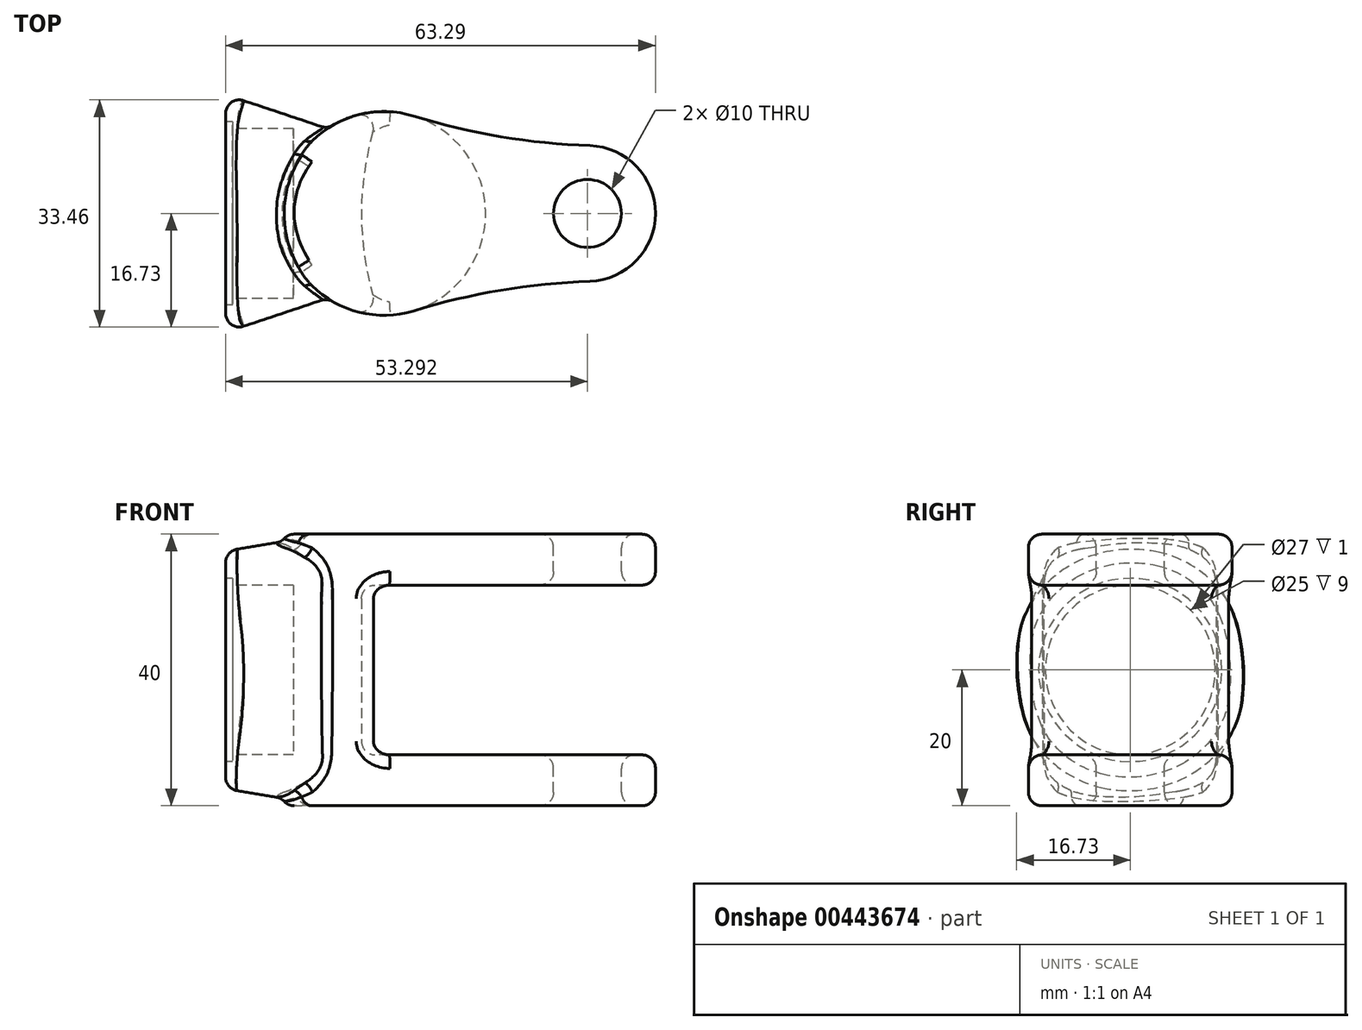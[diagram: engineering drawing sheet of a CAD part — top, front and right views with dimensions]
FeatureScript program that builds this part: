
annotation { "Feature Type Name" : "Feature", "Feature Type Description" : "" }
export const myFeature = defineFeature(function(context is Context, id is Id, definition is map)
    precondition{}
    {
        {
            var Q0;
            Q0=qCreatedBy(makeId("Right.planeOp"),FACE);
            var sketch = newSketch(context, id + "F0", { "sketchPlane" : qUnion([Q0])});
            skCircle(sketch, "E0", {"center": v(0, 0) * mm, "radius": 17.5 * mm});
            skSolve(sketch);
        }
        {
            var Q0;
            Q0=makeQuery(id+"F0.imprint","IMPRINT",FACE,{"disambiguationData":[TD([[makeQuery(id+"F0.imprint","IMPRINT",EDGE,{"derivedFrom":sQuery(id+"F0.wireOp",EDGE,"E0")}),1.0]])]});
            cPlane(context, id + "F1", {"entities" : qUnion([Q0]), "cplaneType" : CPlaneType.OFFSET, "offset" : 15 * mm, "width" : 150 * mm, "height" : 150 * mm});
        }
        {
            var Q0;
            Q0=qCreatedBy(id+"F1.planeOp",FACE);
            var sketch = newSketch(context, id + "F2", { "sketchPlane" : qUnion([Q0])});
            skLineSegment(sketch, "E1.bottom", {"start": v(-5, -20) * mm, "end": v(5, -20) * mm});
            skLineSegment(sketch, "E1.top", {"start": v(-5, 20) * mm, "end": v(5, 20) * mm});
            skLineSegment(sketch, "E1.left", {"start": v(-12.5, -12.5) * mm, "end": v(-12.5, 12.5) * mm});
            skLineSegment(sketch, "E1.right", {"start": v(12.5, -12.5) * mm, "end": v(12.5, 12.5) * mm});
            skPoint(sketch, "E1.middle", {"position": v(0, 0) * mm});
            skPoint(sketch, "E2.visualSharp", {"position": v(-12.5, -20) * mm});
            skArc(sketch, "E2.filletArc", {"start": v(-12.5, -12.5) * mm, "mid": v(-10.3, -17.8) * mm, "end": v(-5, -20) * mm});
            skPoint(sketch, "E3.visualSharp", {"position": v(12.5, -20) * mm});
            skArc(sketch, "E3.filletArc", {"start": v(5, -20) * mm, "mid": v(10.3, -17.8) * mm, "end": v(12.5, -12.5) * mm});
            skPoint(sketch, "E4.visualSharp", {"position": v(-12.5, 20) * mm});
            skArc(sketch, "E4.filletArc", {"start": v(-5, 20) * mm, "mid": v(-10.3, 17.8) * mm, "end": v(-12.5, 12.5) * mm});
            skPoint(sketch, "E5.visualSharp", {"position": v(12.5, 20) * mm});
            skArc(sketch, "E5.filletArc", {"start": v(12.5, 12.5) * mm, "mid": v(10.3, 17.8) * mm, "end": v(5, 20) * mm});
            skSolve(sketch);
        }
        {
            var Q0;
            Q0=makeQuery(id+"F0.imprint","IMPRINT",FACE,{"disambiguationData":[TD([[makeQuery(id+"F0.imprint","IMPRINT",EDGE,{"derivedFrom":sQuery(id+"F0.wireOp",EDGE,"E0")}),1.0]])]});
            var Q1;
            Q1=makeQuery(id+"F2.imprint","IMPRINT",FACE,{"disambiguationData":[TD([[makeQuery(id+"F2.imprint","IMPRINT",EDGE,{"derivedFrom":sQuery(id+"F2.wireOp",EDGE,"E1.bottom")}),1.0]])]});
            loft(context, id + "F3", {"sheetProfilesArray" : [{ "sheetProfileEntities" : qUnion([Q0]) }, { "sheetProfileEntities" : qUnion([Q1]) }]});
        }
        {
            var Q0;
            Q0=qCreatedBy(makeId("Top.planeOp"),FACE);
            var sketch = newSketch(context, id + "F4", { "sketchPlane" : qUnion([Q0])});
            skArc(sketch, "E6", {"start": v(27.7, 14.34) * mm, "mid": v(8.3, 0) * mm, "end": v(27.7, -14.34) * mm});
            skArc(sketch, "E7", {"start": v(53.63, -10) * mm, "mid": v(63.3, 0) * mm, "end": v(53.63, 10) * mm});
            skLineSegment(sketch, "E8", {"start": v(23.3, 0) * mm, "end": v(53.3, 0) * mm, "construction": true});
            skArc(sketch, "E9", {"start": v(27.7, 14.34) * mm, "mid": v(40.52, 11.31) * mm, "end": v(53.63, 10) * mm});
            skArc(sketch, "E10.MirrorCS", {"start": v(27.7, -14.34) * mm, "mid": v(40.52, -11.31) * mm, "end": v(53.63, -10) * mm});
            skSolve(sketch);
        }
        {
            var Q0;
            Q0 = qSketchRegion(id + "F4", true);
            extrude(context, id + "F5", {"entities" : qUnion([Q0]), "operationType" : NewBodyOperationType.ADD, "endBound" : BoundingType.SYMMETRIC, "depth" : 40 * mm});
        }
        {
            var Q0;
            Q0=qCreatedBy(makeId("Front.planeOp"),FACE);
            var sketch = newSketch(context, id + "F6", { "sketchPlane" : qUnion([Q0])});
            skLineSegment(sketch, "E11.bottom", {"start": v(20, 12.5) * mm, "end": v(63.3, 12.5) * mm});
            skLineSegment(sketch, "E11.top", {"start": v(20, -12.5) * mm, "end": v(63.3, -12.5) * mm});
            skLineSegment(sketch, "E11.left", {"start": v(20, 12.5) * mm, "end": v(20, -12.5) * mm});
            skLineSegment(sketch, "E11.right", {"start": v(63.3, 12.5) * mm, "end": v(63.3, -12.5) * mm});
            skSolve(sketch);
        }
        {
            var Q0;
            Q0 = qSketchRegion(id + "F6", true);
            var Q1;
            Q1=sQuery(id+"F6.wireOp",EDGE,"E11.right");
            revolve(context, id + "F7", {"operationType" : NewBodyOperationType.REMOVE, "entities" : qUnion([Q0]), "axis" : qUnion([Q1]), "revolveType" : RevolveType.FULL, "oppositeDirection" : true});
        }
        {
            var Q0;
            Q0=makeQuery(id+"F3.opLoft","CAP_FACE",FACE,{"disambiguationData":[OSD([makeQuery(id+"F0.imprint","IMPRINT",FACE,{"disambiguationData":[TD([[makeQuery(id+"F0.imprint","IMPRINT",EDGE,{"derivedFrom":sQuery(id+"F0.wireOp",EDGE,"E0")}),1.0]])]})])],"isStart":true});
            var sketch = newSketch(context, id + "F8", { "sketchPlane" : qUnion([Q0])});
            skCircle(sketch, "E12", {"center": v(0, 0) * mm, "radius": 12.5 * mm});
            skSolve(sketch);
        }
        {
            var Q0;
            Q0 = qSketchRegion(id + "F8", true);
            extrude(context, id + "F9", {"entities" : qUnion([Q0]), "operationType" : NewBodyOperationType.REMOVE, "oppositeDirection" : true, "depth" : 10 * mm});
        }
        {
            var Q0;
            Q0=makeQuery(id+"F3.opLoft","CAP_FACE",FACE,{"disambiguationData":[OSD([makeQuery(id+"F0.imprint","IMPRINT",FACE,{"disambiguationData":[TD([[makeQuery(id+"F0.imprint","IMPRINT",EDGE,{"derivedFrom":sQuery(id+"F0.wireOp",EDGE,"E0")}),1.0]])]})])],"isStart":true});
            var sketch = newSketch(context, id + "F10", { "sketchPlane" : qUnion([Q0])});
            skCircle(sketch, "E13.0", {"center": v(0, 0) * mm, "radius": 13.5 * mm});
            skSolve(sketch);
        }
        {
            var Q0;
            Q0 = qSketchRegion(id + "F10", true);
            extrude(context, id + "F11", {"entities" : qUnion([Q0]), "operationType" : NewBodyOperationType.REMOVE, "oppositeDirection" : true, "depth" : 1 * mm});
        }
        {
            var Q0;
            Q0=makeQuery(id+"F5.opExtrude","CAP_FACE",FACE,{"disambiguationData":[OSD([sQuery(id+"F4.wireOp",EDGE,"E6"),sQuery(id+"F4.wireOp",EDGE,"E7"),sQuery(id+"F4.wireOp",EDGE,"E9"),sQuery(id+"F4.wireOp",EDGE,"E10.MirrorCS")])],"isStart":false});
            var sketch = newSketch(context, id + "F12", { "sketchPlane" : qUnion([Q0])});
            skCircle(sketch, "E14", {"center": v(53.3, 0) * mm, "radius": 5 * mm});
            skSolve(sketch);
        }
        {
            var Q0;
            Q0=makeQuery(id+"F12.imprint","IMPRINT",FACE,{"disambiguationData":[TD([[makeQuery(id+"F12.imprint","IMPRINT",EDGE,{"derivedFrom":sQuery(id+"F12.wireOp",EDGE,"E14")}),1.0]])]});
            extrude(context, id + "F13", {"entities" : qUnion([Q0]), "operationType" : NewBodyOperationType.REMOVE, "endBound" : BoundingType.THROUGH_ALL, "oppositeDirection" : true, "depth" : 25 * mm});
        }
        {
            var Q0;
            Q0=makeQuery(id+"F5.opExtrude","CAP_FACE",FACE,{"disambiguationData":[OSD([sQuery(id+"F4.wireOp",EDGE,"E6"),sQuery(id+"F4.wireOp",EDGE,"E7"),sQuery(id+"F4.wireOp",EDGE,"E9"),sQuery(id+"F4.wireOp",EDGE,"E10.MirrorCS")])],"isStart":false});
            var Q1;
            Q1=makeQuery(id+"F5.opExtrude","CAP_FACE",FACE,{"disambiguationData":[OSD([sQuery(id+"F4.wireOp",EDGE,"E6"),sQuery(id+"F4.wireOp",EDGE,"E7"),sQuery(id+"F4.wireOp",EDGE,"E9"),sQuery(id+"F4.wireOp",EDGE,"E10.MirrorCS")])],"isStart":true});
            var Q2;
            Q2=makeQuery(id+"F7.boolean.opBoolean","COPY",EDGE,{"derivedFrom":makeQuery(id+"F7.opRevolve","SWEPT_EDGE",EDGE,{"disambiguationData":[OSD([sQuery(id+"F6.wireOp",EDGE,"E11.bottom"),sQuery(id+"F6.wireOp",EDGE,"E11.left")])]})});
            var Q3;
            Q3=makeQuery(id+"F7.boolean.opBoolean","COPY",EDGE,{"derivedFrom":makeQuery(id+"F7.opRevolve","SWEPT_EDGE",EDGE,{"disambiguationData":[OSD([sQuery(id+"F6.wireOp",EDGE,"E11.top"),sQuery(id+"F6.wireOp",EDGE,"E11.left")])]})});
            fillet(context, id + "F14", {"entities" : qUnion([Q0, Q1, Q2, Q3]), "radius" : 2 * mm, "tangentPropagation" : true, "allowEdgeOverflow" : false});
        }
        {
            var Q0;
            Q0=makeQuery(id+"F7.boolean.opBoolean","COPY",FACE,{"derivedFrom":makeQuery(id+"F7.opRevolve","SWEPT_FACE",FACE,{"disambiguationData":[OSD([sQuery(id+"F6.wireOp",EDGE,"E11.top")])]})});
            var Q1;
            Q1=makeQuery(id+"F7.boolean.opBoolean","COPY",FACE,{"derivedFrom":makeQuery(id+"F7.opRevolve","SWEPT_FACE",FACE,{"disambiguationData":[OSD([sQuery(id+"F6.wireOp",EDGE,"E11.bottom")])]})});
            fillet(context, id + "F15", {"entities" : qUnion([Q0, Q1]), "radius" : 2 * mm, "tangentPropagation" : true, "allowEdgeOverflow" : false});
        }
        {
            var Q0;
            Q0=makeQuery(id+"F3.opLoft","MID_CAP_EDGE",EDGE,{"disambiguationData":[OSD([sQuery(id+"F2.wireOp",EDGE,"E1.right"),sQuery(id+"F2.wireOp",EDGE,"E3.filletArc"),sQuery(id+"F2.wireOp",EDGE,"E5.filletArc")])],"capPos":1.0});
            var Q1;
            Q1=makeQuery(id+"F5.boolean.opBoolean","INTERSECT",EDGE,{"disambiguationData":[OD(1.0)],"derivedFrom":[makeQuery(id+"F3.opLoft","SWEPT_FACE",FACE,{"disambiguationData":[OSD([sQuery(id+"F0.wireOp",EDGE,"E0"),sQuery(id+"F2.wireOp",EDGE,"E1.bottom"),sQuery(id+"F2.wireOp",EDGE,"E2.filletArc"),sQuery(id+"F2.wireOp",EDGE,"E3.filletArc")])]}),makeQuery(id+"F5.opExtrude","SWEPT_FACE",FACE,{"disambiguationData":[OSD([sQuery(id+"F4.wireOp",EDGE,"E6")])]})]});
            var Q2;
            Q2=makeQuery(id+"F3.opLoft","SWEPT_FACE",FACE,{"disambiguationData":[OSD([sQuery(id+"F0.wireOp",EDGE,"E0"),sQuery(id+"F2.wireOp",EDGE,"E1.bottom"),sQuery(id+"F2.wireOp",EDGE,"E2.filletArc"),sQuery(id+"F2.wireOp",EDGE,"E3.filletArc")])]});
            fillet(context, id + "F16", {"entities" : qUnion([Q0, Q1, Q2]), "radius" : 2 * mm, "tangentPropagation" : true, "allowEdgeOverflow" : false});
        }
    });
